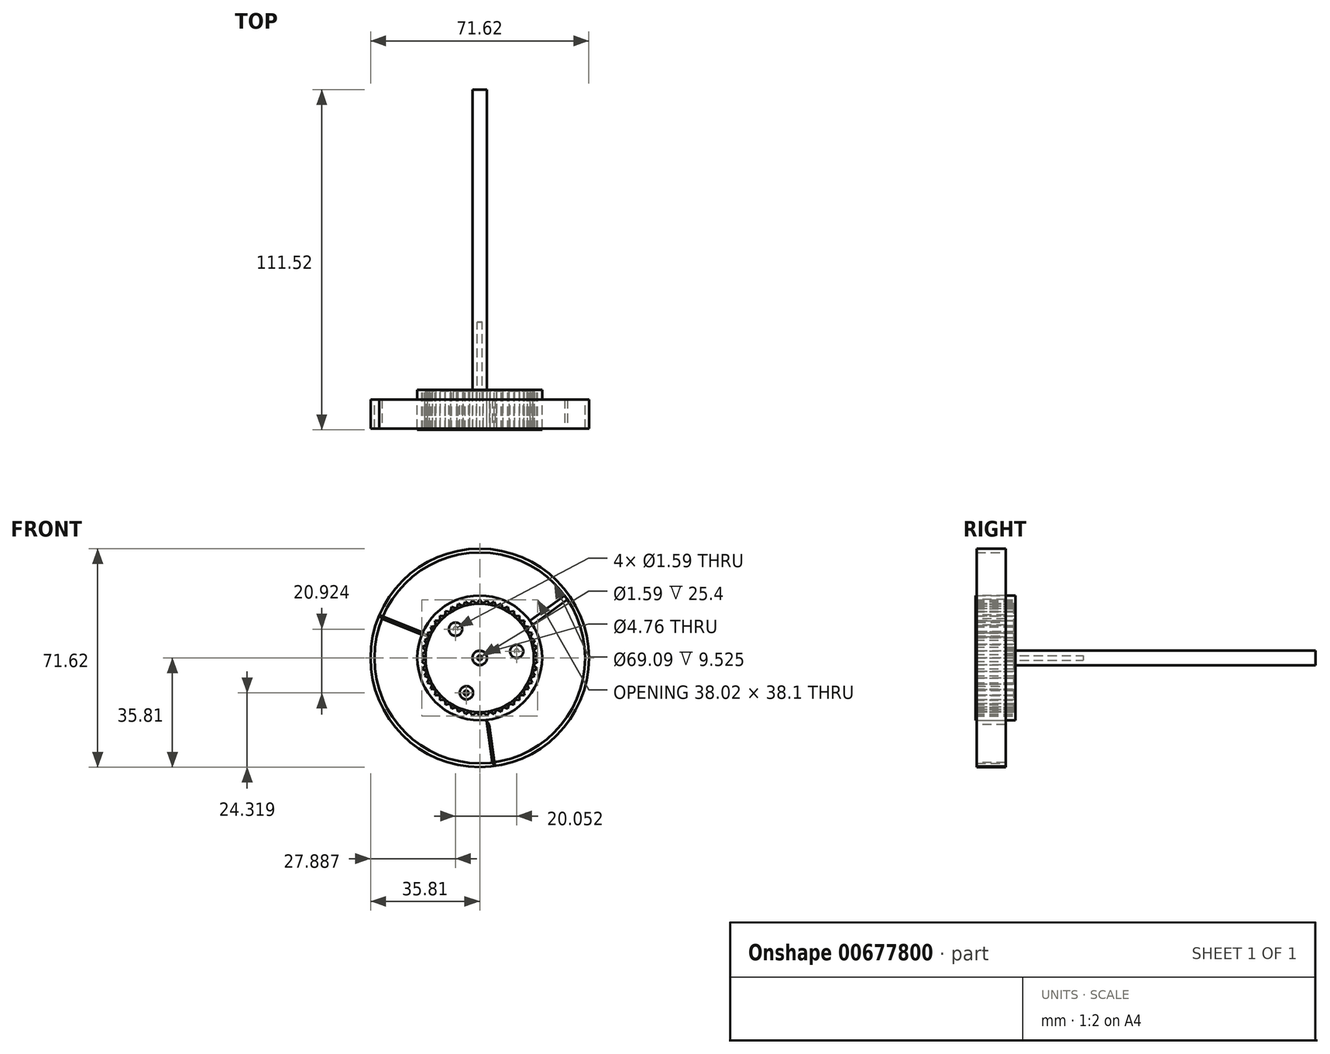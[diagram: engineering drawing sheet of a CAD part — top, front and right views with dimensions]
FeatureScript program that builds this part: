
annotation { "Feature Type Name" : "Feature", "Feature Type Description" : "" }
export const myFeature = defineFeature(function(context is Context, id is Id, definition is map)
    precondition{}
    {
        {
            var Q0;
            Q0=qCreatedBy(makeId("Front.planeOp"),FACE);
            var sketch = newSketch(context, id + "F0", { "sketchPlane" : qUnion([Q0])});
            skCircle(sketch, "E0.cCircle", {"center": v(0, 0) * mm, "radius": 19.01 * mm, "construction": true});
            skLineSegment(sketch, "E0.0", {"start": v(19.01, 1.2) * mm, "end": v(19.01, -1.2) * mm});
            skLineSegment(sketch, "E0.1", {"start": v(19.01, -1.2) * mm, "end": v(18.71, -3.57) * mm});
            skLineSegment(sketch, "E0.2", {"start": v(18.71, -3.57) * mm, "end": v(18.12, -5.89) * mm});
            skLineSegment(sketch, "E0.3", {"start": v(18.12, -5.89) * mm, "end": v(17.24, -8.11) * mm});
            skLineSegment(sketch, "E0.4", {"start": v(17.24, -8.11) * mm, "end": v(16.08, -10.2) * mm});
            skLineSegment(sketch, "E0.5", {"start": v(16.08, -10.2) * mm, "end": v(14.68, -12.14) * mm});
            skLineSegment(sketch, "E0.6", {"start": v(14.68, -12.14) * mm, "end": v(13.04, -13.89) * mm});
            skLineSegment(sketch, "E0.7", {"start": v(13.04, -13.89) * mm, "end": v(11.2, -15.41) * mm});
            skLineSegment(sketch, "E0.8", {"start": v(11.2, -15.41) * mm, "end": v(9.18, -16.7) * mm});
            skLineSegment(sketch, "E0.9", {"start": v(9.18, -16.7) * mm, "end": v(7.01, -17.71) * mm});
            skLineSegment(sketch, "E0.10", {"start": v(7.01, -17.71) * mm, "end": v(4.74, -18.45) * mm});
            skLineSegment(sketch, "E0.11", {"start": v(4.74, -18.45) * mm, "end": v(2.39, -18.9) * mm});
            skLineSegment(sketch, "E0.12", {"start": v(2.39, -18.9) * mm, "end": v(0, -19.05) * mm});
            skLineSegment(sketch, "E0.13", {"start": v(0, -19.05) * mm, "end": v(-2.39, -18.9) * mm});
            skLineSegment(sketch, "E0.14", {"start": v(-2.39, -18.9) * mm, "end": v(-4.74, -18.45) * mm});
            skLineSegment(sketch, "E0.15", {"start": v(-4.74, -18.45) * mm, "end": v(-7.01, -17.71) * mm});
            skLineSegment(sketch, "E0.16", {"start": v(-7.01, -17.71) * mm, "end": v(-9.18, -16.7) * mm});
            skLineSegment(sketch, "E0.17", {"start": v(-9.18, -16.7) * mm, "end": v(-11.2, -15.41) * mm});
            skLineSegment(sketch, "E0.18", {"start": v(-11.2, -15.41) * mm, "end": v(-13.04, -13.89) * mm});
            skLineSegment(sketch, "E0.19", {"start": v(-13.04, -13.89) * mm, "end": v(-14.68, -12.14) * mm});
            skLineSegment(sketch, "E0.20", {"start": v(-14.68, -12.14) * mm, "end": v(-16.08, -10.2) * mm});
            skLineSegment(sketch, "E0.21", {"start": v(-16.08, -10.2) * mm, "end": v(-17.24, -8.11) * mm});
            skLineSegment(sketch, "E0.22", {"start": v(-17.24, -8.11) * mm, "end": v(-18.12, -5.89) * mm});
            skLineSegment(sketch, "E0.23", {"start": v(-18.12, -5.89) * mm, "end": v(-18.71, -3.57) * mm});
            skLineSegment(sketch, "E0.24", {"start": v(-18.71, -3.57) * mm, "end": v(-19.01, -1.2) * mm});
            skLineSegment(sketch, "E0.25", {"start": v(-19.01, -1.2) * mm, "end": v(-19.01, 1.2) * mm});
            skLineSegment(sketch, "E0.26", {"start": v(-19.01, 1.2) * mm, "end": v(-18.71, 3.57) * mm});
            skLineSegment(sketch, "E0.27", {"start": v(-18.71, 3.57) * mm, "end": v(-18.12, 5.89) * mm});
            skLineSegment(sketch, "E0.28", {"start": v(-18.12, 5.89) * mm, "end": v(-17.24, 8.11) * mm});
            skLineSegment(sketch, "E0.29", {"start": v(-17.24, 8.11) * mm, "end": v(-16.08, 10.2) * mm});
            skLineSegment(sketch, "E0.30", {"start": v(-16.08, 10.2) * mm, "end": v(-14.68, 12.14) * mm});
            skLineSegment(sketch, "E0.31", {"start": v(-14.68, 12.14) * mm, "end": v(-13.04, 13.89) * mm});
            skLineSegment(sketch, "E0.32", {"start": v(-13.04, 13.89) * mm, "end": v(-11.2, 15.41) * mm});
            skLineSegment(sketch, "E0.33", {"start": v(-11.2, 15.41) * mm, "end": v(-9.18, 16.7) * mm});
            skLineSegment(sketch, "E0.34", {"start": v(-9.18, 16.7) * mm, "end": v(-7.01, 17.71) * mm});
            skLineSegment(sketch, "E0.35", {"start": v(-7.01, 17.71) * mm, "end": v(-4.74, 18.45) * mm});
            skLineSegment(sketch, "E0.36", {"start": v(-4.74, 18.45) * mm, "end": v(-2.39, 18.9) * mm});
            skLineSegment(sketch, "E0.37", {"start": v(-2.39, 18.9) * mm, "end": v(0, 19.05) * mm});
            skLineSegment(sketch, "E0.38", {"start": v(0, 19.05) * mm, "end": v(2.39, 18.9) * mm});
            skLineSegment(sketch, "E0.39", {"start": v(2.39, 18.9) * mm, "end": v(4.74, 18.45) * mm});
            skLineSegment(sketch, "E0.40", {"start": v(4.74, 18.45) * mm, "end": v(7.01, 17.71) * mm});
            skLineSegment(sketch, "E0.41", {"start": v(7.01, 17.71) * mm, "end": v(9.18, 16.7) * mm});
            skLineSegment(sketch, "E0.42", {"start": v(9.18, 16.7) * mm, "end": v(11.2, 15.41) * mm});
            skLineSegment(sketch, "E0.43", {"start": v(11.2, 15.41) * mm, "end": v(13.04, 13.89) * mm});
            skLineSegment(sketch, "E0.44", {"start": v(13.04, 13.89) * mm, "end": v(14.68, 12.14) * mm});
            skLineSegment(sketch, "E0.45", {"start": v(14.68, 12.14) * mm, "end": v(16.08, 10.2) * mm});
            skLineSegment(sketch, "E0.46", {"start": v(16.08, 10.2) * mm, "end": v(17.24, 8.11) * mm});
            skLineSegment(sketch, "E0.47", {"start": v(17.24, 8.11) * mm, "end": v(18.12, 5.89) * mm});
            skLineSegment(sketch, "E0.48", {"start": v(18.12, 5.89) * mm, "end": v(18.71, 3.57) * mm});
            skLineSegment(sketch, "E0.49", {"start": v(18.71, 3.57) * mm, "end": v(19.01, 1.2) * mm});
            skPoint(sketch, "E0.0.midPoint", {"position": v(19.01, 0) * mm});
            skCircle(sketch, "E1", {"center": v(0, 0) * mm, "radius": 20.47 * mm});
            skCircle(sketch, "E2", {"center": v(0, 0) * mm, "radius": 2.38 * mm});
            skCircle(sketch, "E3", {"center": v(0, 0) * mm, "radius": 17.76 * mm});
            skSolve(sketch);
        }
        {
            var Q0;
            Q0=makeQuery(id+"F0.imprint","IMPRINT",FACE,{"disambiguationData":[TD([[makeQuery(id+"F0.imprint","IMPRINT",EDGE,{"derivedFrom":sQuery(id+"F0.wireOp",EDGE,"E0.0")}),1.0]])]});
            extrude(context, id + "F1", {"entities" : qUnion([Q0]), "depth" : 9.92 * mm, "offsetDistance" : 25.4 * mm});
        }
        {
            var Q0;
            Q0=makeQuery(id+"F0.imprint","IMPRINT",FACE,{"disambiguationData":[TD([[makeQuery(id+"F0.imprint","IMPRINT",EDGE,{"derivedFrom":sQuery(id+"F0.wireOp",EDGE,"E0.0")}),1.0]])]});
            extrude(context, id + "F2", {"entities" : qUnion([Q0]), "operationType" : NewBodyOperationType.ADD, "oppositeDirection" : true, "depth" : 3.17 * mm, "offsetDistance" : 25.4 * mm});
        }
        {
            var Q0;
            Q0=makeQuery(id+"F0.imprint","IMPRINT",FACE,{"disambiguationData":[TD([[makeQuery(id+"F0.imprint","IMPRINT",EDGE,{"derivedFrom":sQuery(id+"F0.wireOp",EDGE,"E2")}),1.0]])]});
            extrude(context, id + "F3", {"entities" : qUnion([Q0]), "oppositeDirection" : true, "depth" : 101.6 * mm, "offsetDistance" : 25.4 * mm});
        }
        {
            var Q0;
            {var subQ0=sQuery(id+"F0.wireOp",EDGE,"E0.9");Q0=makeQuery(id+"F2.boolean.opBoolean","MERGE",FACE,{"derivedFrom":[makeQuery(id+"F1.opExtrude","SWEPT_FACE",FACE,{"disambiguationData":[OSD([subQ0])]}),makeQuery(id+"F2.opExtrude","SWEPT_FACE",FACE,{"disambiguationData":[OSD([subQ0])]})]});}
            extrude(context, id + "F4", {"entities" : qUnion([Q0]), "operationType" : NewBodyOperationType.ADD, "depth" : 1.2 * mm, "offsetDistance" : 25.4 * mm});
        }
        {
            var Q0;
            {var subQ0=sQuery(id+"F0.wireOp",EDGE,"E0.11");Q0=makeQuery(id+"F2.boolean.opBoolean","MERGE",FACE,{"derivedFrom":[makeQuery(id+"F1.opExtrude","SWEPT_FACE",FACE,{"disambiguationData":[OSD([subQ0])]}),makeQuery(id+"F2.opExtrude","SWEPT_FACE",FACE,{"disambiguationData":[OSD([subQ0])]})]});}
            extrude(context, id + "F5", {"entities" : qUnion([Q0]), "operationType" : NewBodyOperationType.ADD, "depth" : 1.2 * mm, "offsetDistance" : 25.4 * mm});
        }
        {
            var Q0;
            {var subQ0=sQuery(id+"F0.wireOp",EDGE,"E0.13");Q0=makeQuery(id+"F2.boolean.opBoolean","MERGE",FACE,{"derivedFrom":[makeQuery(id+"F1.opExtrude","SWEPT_FACE",FACE,{"disambiguationData":[OSD([subQ0])]}),makeQuery(id+"F2.opExtrude","SWEPT_FACE",FACE,{"disambiguationData":[OSD([subQ0])]})]});}
            extrude(context, id + "F6", {"entities" : qUnion([Q0]), "operationType" : NewBodyOperationType.ADD, "depth" : 1.2 * mm, "offsetDistance" : 25.4 * mm});
        }
        {
            var Q0;
            {var subQ0=sQuery(id+"F0.wireOp",EDGE,"E0.7");Q0=makeQuery(id+"F2.boolean.opBoolean","MERGE",FACE,{"derivedFrom":[makeQuery(id+"F1.opExtrude","SWEPT_FACE",FACE,{"disambiguationData":[OSD([subQ0])]}),makeQuery(id+"F2.opExtrude","SWEPT_FACE",FACE,{"disambiguationData":[OSD([subQ0])]})]});}
            extrude(context, id + "F7", {"entities" : qUnion([Q0]), "operationType" : NewBodyOperationType.ADD, "depth" : 1.2 * mm, "offsetDistance" : 25.4 * mm});
        }
        {
            var Q0;
            {var subQ0=sQuery(id+"F0.wireOp",EDGE,"E0.5");Q0=makeQuery(id+"F2.boolean.opBoolean","MERGE",FACE,{"derivedFrom":[makeQuery(id+"F1.opExtrude","SWEPT_FACE",FACE,{"disambiguationData":[OSD([subQ0])]}),makeQuery(id+"F2.opExtrude","SWEPT_FACE",FACE,{"disambiguationData":[OSD([subQ0])]})]});}
            extrude(context, id + "F8", {"entities" : qUnion([Q0]), "operationType" : NewBodyOperationType.ADD, "depth" : 1.2 * mm, "offsetDistance" : 25.4 * mm});
        }
        {
            var Q0;
            {var subQ0=sQuery(id+"F0.wireOp",EDGE,"E0.3");Q0=makeQuery(id+"F2.boolean.opBoolean","MERGE",FACE,{"derivedFrom":[makeQuery(id+"F1.opExtrude","SWEPT_FACE",FACE,{"disambiguationData":[OSD([subQ0])]}),makeQuery(id+"F2.opExtrude","SWEPT_FACE",FACE,{"disambiguationData":[OSD([subQ0])]})]});}
            extrude(context, id + "F9", {"entities" : qUnion([Q0]), "operationType" : NewBodyOperationType.ADD, "depth" : 1.2 * mm, "offsetDistance" : 25.4 * mm});
        }
        {
            var Q0;
            {var subQ0=sQuery(id+"F0.wireOp",EDGE,"E0.1");Q0=makeQuery(id+"F2.boolean.opBoolean","MERGE",FACE,{"derivedFrom":[makeQuery(id+"F1.opExtrude","SWEPT_FACE",FACE,{"disambiguationData":[OSD([subQ0])]}),makeQuery(id+"F2.opExtrude","SWEPT_FACE",FACE,{"disambiguationData":[OSD([subQ0])]})]});}
            extrude(context, id + "F10", {"entities" : qUnion([Q0]), "operationType" : NewBodyOperationType.ADD, "depth" : 1.2 * mm, "offsetDistance" : 25.4 * mm});
        }
        {
            var Q0;
            {var subQ0=sQuery(id+"F0.wireOp",EDGE,"E0.49");Q0=makeQuery(id+"F2.boolean.opBoolean","MERGE",FACE,{"derivedFrom":[makeQuery(id+"F1.opExtrude","SWEPT_FACE",FACE,{"disambiguationData":[OSD([subQ0])]}),makeQuery(id+"F2.opExtrude","SWEPT_FACE",FACE,{"disambiguationData":[OSD([subQ0])]})]});}
            extrude(context, id + "F11", {"entities" : qUnion([Q0]), "operationType" : NewBodyOperationType.ADD, "depth" : 1.2 * mm, "offsetDistance" : 25.4 * mm});
        }
        {
            var Q0;
            {var subQ0=sQuery(id+"F0.wireOp",EDGE,"E0.47");Q0=makeQuery(id+"F2.boolean.opBoolean","MERGE",FACE,{"derivedFrom":[makeQuery(id+"F1.opExtrude","SWEPT_FACE",FACE,{"disambiguationData":[OSD([subQ0])]}),makeQuery(id+"F2.opExtrude","SWEPT_FACE",FACE,{"disambiguationData":[OSD([subQ0])]})]});}
            extrude(context, id + "F12", {"entities" : qUnion([Q0]), "operationType" : NewBodyOperationType.ADD, "depth" : 1.2 * mm, "offsetDistance" : 25.4 * mm});
        }
        {
            var Q0;
            {var subQ0=sQuery(id+"F0.wireOp",EDGE,"E0.45");Q0=makeQuery(id+"F2.boolean.opBoolean","MERGE",FACE,{"derivedFrom":[makeQuery(id+"F1.opExtrude","SWEPT_FACE",FACE,{"disambiguationData":[OSD([subQ0])]}),makeQuery(id+"F2.opExtrude","SWEPT_FACE",FACE,{"disambiguationData":[OSD([subQ0])]})]});}
            extrude(context, id + "F13", {"entities" : qUnion([Q0]), "operationType" : NewBodyOperationType.ADD, "depth" : 1.2 * mm, "offsetDistance" : 25.4 * mm});
        }
        {
            var Q0;
            {var subQ0=sQuery(id+"F0.wireOp",EDGE,"E0.43");Q0=makeQuery(id+"F2.boolean.opBoolean","MERGE",FACE,{"derivedFrom":[makeQuery(id+"F1.opExtrude","SWEPT_FACE",FACE,{"disambiguationData":[OSD([subQ0])]}),makeQuery(id+"F2.opExtrude","SWEPT_FACE",FACE,{"disambiguationData":[OSD([subQ0])]})]});}
            extrude(context, id + "F14", {"entities" : qUnion([Q0]), "operationType" : NewBodyOperationType.ADD, "depth" : 1.2 * mm, "offsetDistance" : 25.4 * mm});
        }
        {
            var Q0;
            {var subQ0=sQuery(id+"F0.wireOp",EDGE,"E0.41");Q0=makeQuery(id+"F2.boolean.opBoolean","MERGE",FACE,{"derivedFrom":[makeQuery(id+"F1.opExtrude","SWEPT_FACE",FACE,{"disambiguationData":[OSD([subQ0])]}),makeQuery(id+"F2.opExtrude","SWEPT_FACE",FACE,{"disambiguationData":[OSD([subQ0])]})]});}
            extrude(context, id + "F15", {"entities" : qUnion([Q0]), "operationType" : NewBodyOperationType.ADD, "depth" : 1.2 * mm, "offsetDistance" : 25.4 * mm});
        }
        {
            var Q0;
            {var subQ0=sQuery(id+"F0.wireOp",EDGE,"E0.39");Q0=makeQuery(id+"F2.boolean.opBoolean","MERGE",FACE,{"derivedFrom":[makeQuery(id+"F1.opExtrude","SWEPT_FACE",FACE,{"disambiguationData":[OSD([subQ0])]}),makeQuery(id+"F2.opExtrude","SWEPT_FACE",FACE,{"disambiguationData":[OSD([subQ0])]})]});}
            extrude(context, id + "F16", {"entities" : qUnion([Q0]), "operationType" : NewBodyOperationType.ADD, "depth" : 1.2 * mm, "offsetDistance" : 25.4 * mm});
        }
        {
            var Q0;
            {var subQ0=sQuery(id+"F0.wireOp",EDGE,"E0.37");Q0=makeQuery(id+"F2.boolean.opBoolean","MERGE",FACE,{"derivedFrom":[makeQuery(id+"F1.opExtrude","SWEPT_FACE",FACE,{"disambiguationData":[OSD([subQ0])]}),makeQuery(id+"F2.opExtrude","SWEPT_FACE",FACE,{"disambiguationData":[OSD([subQ0])]})]});}
            extrude(context, id + "F17", {"entities" : qUnion([Q0]), "operationType" : NewBodyOperationType.ADD, "depth" : 1.2 * mm, "offsetDistance" : 25.4 * mm});
        }
        {
            var Q0;
            {var subQ0=sQuery(id+"F0.wireOp",EDGE,"E0.35");Q0=makeQuery(id+"F2.boolean.opBoolean","MERGE",FACE,{"derivedFrom":[makeQuery(id+"F1.opExtrude","SWEPT_FACE",FACE,{"disambiguationData":[OSD([subQ0])]}),makeQuery(id+"F2.opExtrude","SWEPT_FACE",FACE,{"disambiguationData":[OSD([subQ0])]})]});}
            extrude(context, id + "F18", {"entities" : qUnion([Q0]), "operationType" : NewBodyOperationType.ADD, "depth" : 1.2 * mm, "offsetDistance" : 25.4 * mm});
        }
        {
            var Q0;
            {var subQ0=sQuery(id+"F0.wireOp",EDGE,"E0.33");Q0=makeQuery(id+"F2.boolean.opBoolean","MERGE",FACE,{"derivedFrom":[makeQuery(id+"F1.opExtrude","SWEPT_FACE",FACE,{"disambiguationData":[OSD([subQ0])]}),makeQuery(id+"F2.opExtrude","SWEPT_FACE",FACE,{"disambiguationData":[OSD([subQ0])]})]});}
            extrude(context, id + "F19", {"entities" : qUnion([Q0]), "operationType" : NewBodyOperationType.ADD, "depth" : 1.2 * mm, "offsetDistance" : 25.4 * mm});
        }
        {
            var Q0;
            {var subQ0=sQuery(id+"F0.wireOp",EDGE,"E0.31");Q0=makeQuery(id+"F2.boolean.opBoolean","MERGE",FACE,{"derivedFrom":[makeQuery(id+"F1.opExtrude","SWEPT_FACE",FACE,{"disambiguationData":[OSD([subQ0])]}),makeQuery(id+"F2.opExtrude","SWEPT_FACE",FACE,{"disambiguationData":[OSD([subQ0])]})]});}
            extrude(context, id + "F20", {"entities" : qUnion([Q0]), "operationType" : NewBodyOperationType.ADD, "depth" : 1.2 * mm, "offsetDistance" : 25.4 * mm});
        }
        {
            var Q0;
            {var subQ0=sQuery(id+"F0.wireOp",EDGE,"E0.29");Q0=makeQuery(id+"F2.boolean.opBoolean","MERGE",FACE,{"derivedFrom":[makeQuery(id+"F1.opExtrude","SWEPT_FACE",FACE,{"disambiguationData":[OSD([subQ0])]}),makeQuery(id+"F2.opExtrude","SWEPT_FACE",FACE,{"disambiguationData":[OSD([subQ0])]})]});}
            extrude(context, id + "F21", {"entities" : qUnion([Q0]), "operationType" : NewBodyOperationType.ADD, "depth" : 1.2 * mm, "offsetDistance" : 25.4 * mm});
        }
        {
            var Q0;
            {var subQ0=sQuery(id+"F0.wireOp",EDGE,"E0.27");Q0=makeQuery(id+"F2.boolean.opBoolean","MERGE",FACE,{"derivedFrom":[makeQuery(id+"F1.opExtrude","SWEPT_FACE",FACE,{"disambiguationData":[OSD([subQ0])]}),makeQuery(id+"F2.opExtrude","SWEPT_FACE",FACE,{"disambiguationData":[OSD([subQ0])]})]});}
            extrude(context, id + "F22", {"entities" : qUnion([Q0]), "operationType" : NewBodyOperationType.ADD, "depth" : 1.2 * mm, "offsetDistance" : 25.4 * mm});
        }
        {
            var Q0;
            {var subQ0=sQuery(id+"F0.wireOp",EDGE,"E0.25");Q0=makeQuery(id+"F2.boolean.opBoolean","MERGE",FACE,{"derivedFrom":[makeQuery(id+"F1.opExtrude","SWEPT_FACE",FACE,{"disambiguationData":[OSD([subQ0])]}),makeQuery(id+"F2.opExtrude","SWEPT_FACE",FACE,{"disambiguationData":[OSD([subQ0])]})]});}
            extrude(context, id + "F23", {"entities" : qUnion([Q0]), "operationType" : NewBodyOperationType.ADD, "depth" : 1.2 * mm, "offsetDistance" : 25.4 * mm});
        }
        {
            var Q0;
            {var subQ0=sQuery(id+"F0.wireOp",EDGE,"E0.23");Q0=makeQuery(id+"F2.boolean.opBoolean","MERGE",FACE,{"derivedFrom":[makeQuery(id+"F1.opExtrude","SWEPT_FACE",FACE,{"disambiguationData":[OSD([subQ0])]}),makeQuery(id+"F2.opExtrude","SWEPT_FACE",FACE,{"disambiguationData":[OSD([subQ0])]})]});}
            extrude(context, id + "F24", {"entities" : qUnion([Q0]), "operationType" : NewBodyOperationType.ADD, "depth" : 1.2 * mm, "offsetDistance" : 25.4 * mm});
        }
        {
            var Q0;
            {var subQ0=sQuery(id+"F0.wireOp",EDGE,"E0.21");Q0=makeQuery(id+"F2.boolean.opBoolean","MERGE",FACE,{"derivedFrom":[makeQuery(id+"F1.opExtrude","SWEPT_FACE",FACE,{"disambiguationData":[OSD([subQ0])]}),makeQuery(id+"F2.opExtrude","SWEPT_FACE",FACE,{"disambiguationData":[OSD([subQ0])]})]});}
            extrude(context, id + "F25", {"entities" : qUnion([Q0]), "operationType" : NewBodyOperationType.ADD, "depth" : 1.2 * mm, "offsetDistance" : 25.4 * mm});
        }
        {
            var Q0;
            {var subQ0=sQuery(id+"F0.wireOp",EDGE,"E0.19");Q0=makeQuery(id+"F2.boolean.opBoolean","MERGE",FACE,{"derivedFrom":[makeQuery(id+"F1.opExtrude","SWEPT_FACE",FACE,{"disambiguationData":[OSD([subQ0])]}),makeQuery(id+"F2.opExtrude","SWEPT_FACE",FACE,{"disambiguationData":[OSD([subQ0])]})]});}
            extrude(context, id + "F26", {"entities" : qUnion([Q0]), "operationType" : NewBodyOperationType.ADD, "depth" : 1.2 * mm, "offsetDistance" : 25.4 * mm});
        }
        {
            var Q0;
            {var subQ0=sQuery(id+"F0.wireOp",EDGE,"E0.17");Q0=makeQuery(id+"F2.boolean.opBoolean","MERGE",FACE,{"derivedFrom":[makeQuery(id+"F1.opExtrude","SWEPT_FACE",FACE,{"disambiguationData":[OSD([subQ0])]}),makeQuery(id+"F2.opExtrude","SWEPT_FACE",FACE,{"disambiguationData":[OSD([subQ0])]})]});}
            extrude(context, id + "F27", {"entities" : qUnion([Q0]), "operationType" : NewBodyOperationType.ADD, "depth" : 1.2 * mm, "offsetDistance" : 25.4 * mm});
        }
        {
            var Q0;
            {var subQ0=sQuery(id+"F0.wireOp",EDGE,"E0.15");Q0=makeQuery(id+"F2.boolean.opBoolean","MERGE",FACE,{"derivedFrom":[makeQuery(id+"F1.opExtrude","SWEPT_FACE",FACE,{"disambiguationData":[OSD([subQ0])]}),makeQuery(id+"F2.opExtrude","SWEPT_FACE",FACE,{"disambiguationData":[OSD([subQ0])]})]});}
            extrude(context, id + "F28", {"entities" : qUnion([Q0]), "operationType" : NewBodyOperationType.ADD, "depth" : 1.2 * mm, "offsetDistance" : 25.4 * mm});
        }
        {
            var Q0;
            Q0=makeQuery(id+"F6.opExtrude","CAP_EDGE",EDGE,{"disambiguationData":[OSD([sQuery(id+"F0.wireOp",EDGE,"E0.12"),sQuery(id+"F0.wireOp",EDGE,"E0.13")])],"isStart":false});
            var Q1;
            Q1=makeQuery(id+"F6.opExtrude","CAP_EDGE",EDGE,{"disambiguationData":[OSD([sQuery(id+"F0.wireOp",EDGE,"E0.13"),sQuery(id+"F0.wireOp",EDGE,"E0.14")])],"isStart":false});
            var Q2;
            Q2=makeQuery(id+"F5.opExtrude","CAP_EDGE",EDGE,{"disambiguationData":[OSD([sQuery(id+"F0.wireOp",EDGE,"E0.11"),sQuery(id+"F0.wireOp",EDGE,"E0.12")])],"isStart":false});
            var Q3;
            Q3=makeQuery(id+"F5.opExtrude","CAP_EDGE",EDGE,{"disambiguationData":[OSD([sQuery(id+"F0.wireOp",EDGE,"E0.10"),sQuery(id+"F0.wireOp",EDGE,"E0.11")])],"isStart":false});
            var Q4;
            Q4=makeQuery(id+"F4.opExtrude","CAP_EDGE",EDGE,{"disambiguationData":[OSD([sQuery(id+"F0.wireOp",EDGE,"E0.9"),sQuery(id+"F0.wireOp",EDGE,"E0.10")])],"isStart":false});
            var Q5;
            Q5=makeQuery(id+"F4.opExtrude","CAP_EDGE",EDGE,{"disambiguationData":[OSD([sQuery(id+"F0.wireOp",EDGE,"E0.8"),sQuery(id+"F0.wireOp",EDGE,"E0.9")])],"isStart":false});
            var Q6;
            Q6=makeQuery(id+"F7.opExtrude","CAP_EDGE",EDGE,{"disambiguationData":[OSD([sQuery(id+"F0.wireOp",EDGE,"E0.6"),sQuery(id+"F0.wireOp",EDGE,"E0.7")])],"isStart":false});
            var Q7;
            Q7=makeQuery(id+"F7.opExtrude","CAP_EDGE",EDGE,{"disambiguationData":[OSD([sQuery(id+"F0.wireOp",EDGE,"E0.7"),sQuery(id+"F0.wireOp",EDGE,"E0.8")])],"isStart":false});
            var Q8;
            Q8=makeQuery(id+"F8.opExtrude","CAP_EDGE",EDGE,{"disambiguationData":[OSD([sQuery(id+"F0.wireOp",EDGE,"E0.5"),sQuery(id+"F0.wireOp",EDGE,"E0.6")])],"isStart":false});
            var Q9;
            Q9=makeQuery(id+"F8.opExtrude","CAP_EDGE",EDGE,{"disambiguationData":[OSD([sQuery(id+"F0.wireOp",EDGE,"E0.4"),sQuery(id+"F0.wireOp",EDGE,"E0.5")])],"isStart":false});
            var Q10;
            Q10=makeQuery(id+"F9.opExtrude","CAP_EDGE",EDGE,{"disambiguationData":[OSD([sQuery(id+"F0.wireOp",EDGE,"E0.2"),sQuery(id+"F0.wireOp",EDGE,"E0.3")])],"isStart":false});
            var Q11;
            Q11=makeQuery(id+"F9.opExtrude","CAP_EDGE",EDGE,{"disambiguationData":[OSD([sQuery(id+"F0.wireOp",EDGE,"E0.3"),sQuery(id+"F0.wireOp",EDGE,"E0.4")])],"isStart":false});
            var Q12;
            Q12=makeQuery(id+"F10.opExtrude","CAP_EDGE",EDGE,{"disambiguationData":[OSD([sQuery(id+"F0.wireOp",EDGE,"E0.1"),sQuery(id+"F0.wireOp",EDGE,"E0.2")])],"isStart":false});
            var Q13;
            Q13=makeQuery(id+"F10.opExtrude","CAP_EDGE",EDGE,{"disambiguationData":[OSD([sQuery(id+"F0.wireOp",EDGE,"E0.0"),sQuery(id+"F0.wireOp",EDGE,"E0.1")])],"isStart":false});
            var Q14;
            Q14=makeQuery(id+"F11.opExtrude","CAP_EDGE",EDGE,{"disambiguationData":[OSD([sQuery(id+"F0.wireOp",EDGE,"E0.48"),sQuery(id+"F0.wireOp",EDGE,"E0.49")])],"isStart":false});
            var Q15;
            Q15=makeQuery(id+"F11.opExtrude","CAP_EDGE",EDGE,{"disambiguationData":[OSD([sQuery(id+"F0.wireOp",EDGE,"E0.0"),sQuery(id+"F0.wireOp",EDGE,"E0.49")])],"isStart":false});
            var Q16;
            Q16=makeQuery(id+"F12.opExtrude","CAP_EDGE",EDGE,{"disambiguationData":[OSD([sQuery(id+"F0.wireOp",EDGE,"E0.47"),sQuery(id+"F0.wireOp",EDGE,"E0.48")])],"isStart":false});
            var Q17;
            Q17=makeQuery(id+"F12.opExtrude","CAP_EDGE",EDGE,{"disambiguationData":[OSD([sQuery(id+"F0.wireOp",EDGE,"E0.46"),sQuery(id+"F0.wireOp",EDGE,"E0.47")])],"isStart":false});
            var Q18;
            Q18=makeQuery(id+"F13.opExtrude","CAP_EDGE",EDGE,{"disambiguationData":[OSD([sQuery(id+"F0.wireOp",EDGE,"E0.45"),sQuery(id+"F0.wireOp",EDGE,"E0.46")])],"isStart":false});
            var Q19;
            Q19=makeQuery(id+"F13.opExtrude","CAP_EDGE",EDGE,{"disambiguationData":[OSD([sQuery(id+"F0.wireOp",EDGE,"E0.44"),sQuery(id+"F0.wireOp",EDGE,"E0.45")])],"isStart":false});
            var Q20;
            Q20=makeQuery(id+"F14.opExtrude","CAP_EDGE",EDGE,{"disambiguationData":[OSD([sQuery(id+"F0.wireOp",EDGE,"E0.43"),sQuery(id+"F0.wireOp",EDGE,"E0.44")])],"isStart":false});
            var Q21;
            Q21=makeQuery(id+"F14.opExtrude","CAP_EDGE",EDGE,{"disambiguationData":[OSD([sQuery(id+"F0.wireOp",EDGE,"E0.42"),sQuery(id+"F0.wireOp",EDGE,"E0.43")])],"isStart":false});
            var Q22;
            Q22=makeQuery(id+"F15.opExtrude","CAP_EDGE",EDGE,{"disambiguationData":[OSD([sQuery(id+"F0.wireOp",EDGE,"E0.41"),sQuery(id+"F0.wireOp",EDGE,"E0.42")])],"isStart":false});
            var Q23;
            Q23=makeQuery(id+"F15.opExtrude","CAP_EDGE",EDGE,{"disambiguationData":[OSD([sQuery(id+"F0.wireOp",EDGE,"E0.40"),sQuery(id+"F0.wireOp",EDGE,"E0.41")])],"isStart":false});
            var Q24;
            Q24=makeQuery(id+"F16.opExtrude","CAP_EDGE",EDGE,{"disambiguationData":[OSD([sQuery(id+"F0.wireOp",EDGE,"E0.39"),sQuery(id+"F0.wireOp",EDGE,"E0.40")])],"isStart":false});
            var Q25;
            Q25=makeQuery(id+"F16.opExtrude","CAP_EDGE",EDGE,{"disambiguationData":[OSD([sQuery(id+"F0.wireOp",EDGE,"E0.38"),sQuery(id+"F0.wireOp",EDGE,"E0.39")])],"isStart":false});
            var Q26;
            Q26=makeQuery(id+"F17.opExtrude","CAP_EDGE",EDGE,{"disambiguationData":[OSD([sQuery(id+"F0.wireOp",EDGE,"E0.37"),sQuery(id+"F0.wireOp",EDGE,"E0.38")])],"isStart":false});
            var Q27;
            Q27=makeQuery(id+"F17.opExtrude","CAP_EDGE",EDGE,{"disambiguationData":[OSD([sQuery(id+"F0.wireOp",EDGE,"E0.36"),sQuery(id+"F0.wireOp",EDGE,"E0.37")])],"isStart":false});
            var Q28;
            Q28=makeQuery(id+"F18.opExtrude","CAP_EDGE",EDGE,{"disambiguationData":[OSD([sQuery(id+"F0.wireOp",EDGE,"E0.35"),sQuery(id+"F0.wireOp",EDGE,"E0.36")])],"isStart":false});
            var Q29;
            Q29=makeQuery(id+"F18.opExtrude","CAP_EDGE",EDGE,{"disambiguationData":[OSD([sQuery(id+"F0.wireOp",EDGE,"E0.34"),sQuery(id+"F0.wireOp",EDGE,"E0.35")])],"isStart":false});
            var Q30;
            Q30=makeQuery(id+"F19.opExtrude","CAP_EDGE",EDGE,{"disambiguationData":[OSD([sQuery(id+"F0.wireOp",EDGE,"E0.32"),sQuery(id+"F0.wireOp",EDGE,"E0.33")])],"isStart":false});
            var Q31;
            Q31=makeQuery(id+"F19.opExtrude","CAP_EDGE",EDGE,{"disambiguationData":[OSD([sQuery(id+"F0.wireOp",EDGE,"E0.33"),sQuery(id+"F0.wireOp",EDGE,"E0.34")])],"isStart":false});
            var Q32;
            Q32=makeQuery(id+"F20.opExtrude","CAP_EDGE",EDGE,{"disambiguationData":[OSD([sQuery(id+"F0.wireOp",EDGE,"E0.30"),sQuery(id+"F0.wireOp",EDGE,"E0.31")])],"isStart":false});
            var Q33;
            Q33=makeQuery(id+"F20.opExtrude","CAP_EDGE",EDGE,{"disambiguationData":[OSD([sQuery(id+"F0.wireOp",EDGE,"E0.31"),sQuery(id+"F0.wireOp",EDGE,"E0.32")])],"isStart":false});
            var Q34;
            Q34=makeQuery(id+"F21.opExtrude","CAP_EDGE",EDGE,{"disambiguationData":[OSD([sQuery(id+"F0.wireOp",EDGE,"E0.29"),sQuery(id+"F0.wireOp",EDGE,"E0.30")])],"isStart":false});
            var Q35;
            Q35=makeQuery(id+"F21.opExtrude","CAP_EDGE",EDGE,{"disambiguationData":[OSD([sQuery(id+"F0.wireOp",EDGE,"E0.28"),sQuery(id+"F0.wireOp",EDGE,"E0.29")])],"isStart":false});
            var Q36;
            Q36=makeQuery(id+"F22.opExtrude","CAP_EDGE",EDGE,{"disambiguationData":[OSD([sQuery(id+"F0.wireOp",EDGE,"E0.27"),sQuery(id+"F0.wireOp",EDGE,"E0.28")])],"isStart":false});
            var Q37;
            Q37=makeQuery(id+"F22.opExtrude","CAP_EDGE",EDGE,{"disambiguationData":[OSD([sQuery(id+"F0.wireOp",EDGE,"E0.26"),sQuery(id+"F0.wireOp",EDGE,"E0.27")])],"isStart":false});
            var Q38;
            Q38=makeQuery(id+"F23.opExtrude","CAP_EDGE",EDGE,{"disambiguationData":[OSD([sQuery(id+"F0.wireOp",EDGE,"E0.25"),sQuery(id+"F0.wireOp",EDGE,"E0.26")])],"isStart":false});
            var Q39;
            Q39=makeQuery(id+"F23.opExtrude","CAP_EDGE",EDGE,{"disambiguationData":[OSD([sQuery(id+"F0.wireOp",EDGE,"E0.24"),sQuery(id+"F0.wireOp",EDGE,"E0.25")])],"isStart":false});
            var Q40;
            Q40=makeQuery(id+"F24.opExtrude","CAP_EDGE",EDGE,{"disambiguationData":[OSD([sQuery(id+"F0.wireOp",EDGE,"E0.23"),sQuery(id+"F0.wireOp",EDGE,"E0.24")])],"isStart":false});
            var Q41;
            Q41=makeQuery(id+"F24.opExtrude","CAP_EDGE",EDGE,{"disambiguationData":[OSD([sQuery(id+"F0.wireOp",EDGE,"E0.22"),sQuery(id+"F0.wireOp",EDGE,"E0.23")])],"isStart":false});
            var Q42;
            Q42=makeQuery(id+"F25.opExtrude","CAP_EDGE",EDGE,{"disambiguationData":[OSD([sQuery(id+"F0.wireOp",EDGE,"E0.21"),sQuery(id+"F0.wireOp",EDGE,"E0.22")])],"isStart":false});
            var Q43;
            Q43=makeQuery(id+"F25.opExtrude","CAP_EDGE",EDGE,{"disambiguationData":[OSD([sQuery(id+"F0.wireOp",EDGE,"E0.20"),sQuery(id+"F0.wireOp",EDGE,"E0.21")])],"isStart":false});
            var Q44;
            Q44=makeQuery(id+"F26.opExtrude","CAP_EDGE",EDGE,{"disambiguationData":[OSD([sQuery(id+"F0.wireOp",EDGE,"E0.19"),sQuery(id+"F0.wireOp",EDGE,"E0.20")])],"isStart":false});
            var Q45;
            Q45=makeQuery(id+"F26.opExtrude","CAP_EDGE",EDGE,{"disambiguationData":[OSD([sQuery(id+"F0.wireOp",EDGE,"E0.18"),sQuery(id+"F0.wireOp",EDGE,"E0.19")])],"isStart":false});
            var Q46;
            Q46=makeQuery(id+"F27.opExtrude","CAP_EDGE",EDGE,{"disambiguationData":[OSD([sQuery(id+"F0.wireOp",EDGE,"E0.16"),sQuery(id+"F0.wireOp",EDGE,"E0.17")])],"isStart":false});
            var Q47;
            Q47=makeQuery(id+"F27.opExtrude","CAP_EDGE",EDGE,{"disambiguationData":[OSD([sQuery(id+"F0.wireOp",EDGE,"E0.17"),sQuery(id+"F0.wireOp",EDGE,"E0.18")])],"isStart":false});
            chamfer(context, id + "F29", {"entities" : qUnion([Q0, Q1, Q2, Q3, Q4, Q5, Q6, Q7, Q8, Q9, Q10, Q11, Q12, Q13, Q14, Q15, Q16, Q17, Q18, Q19, Q20, Q21, Q22, Q23, Q24, Q25, Q26, Q27, Q28, Q29, Q30, Q31, Q32, Q33, Q34, Q35, Q36, Q37, Q38, Q39, Q40, Q41, Q42, Q43, Q44, Q45, Q46, Q47]), "width" : 1.2 * mm, "tangentPropagation" : true});
        }
        {
            var Q0;
            Q0=makeQuery(id+"F28.opExtrude","CAP_EDGE",EDGE,{"disambiguationData":[OSD([sQuery(id+"F0.wireOp",EDGE,"E0.14"),sQuery(id+"F0.wireOp",EDGE,"E0.15")])],"isStart":false});
            var Q1;
            Q1=makeQuery(id+"F28.opExtrude","CAP_EDGE",EDGE,{"disambiguationData":[OSD([sQuery(id+"F0.wireOp",EDGE,"E0.15"),sQuery(id+"F0.wireOp",EDGE,"E0.16")])],"isStart":false});
            chamfer(context, id + "F30", {"entities" : qUnion([Q0, Q1]), "width" : 1.2 * mm, "tangentPropagation" : true});
        }
        {
            var Q0;
            {var subQ0=sQuery(id+"F0.wireOp",EDGE,"E0.16");Q0=makeQuery(id+"F2.boolean.opBoolean","MERGE",FACE,{"derivedFrom":[makeQuery(id+"F1.opExtrude","SWEPT_FACE",FACE,{"disambiguationData":[OSD([subQ0])]}),makeQuery(id+"F2.opExtrude","SWEPT_FACE",FACE,{"disambiguationData":[OSD([subQ0])]})]});}
            extrude(context, id + "F31", {"entities" : qUnion([Q0]), "operationType" : NewBodyOperationType.ADD, "depth" : 1.2 * mm, "offsetDistance" : 25.4 * mm});
        }
        {
            var Q0;
            {var subQ0=sQuery(id+"F0.wireOp",EDGE,"E0.14");Q0=makeQuery(id+"F2.boolean.opBoolean","MERGE",FACE,{"derivedFrom":[makeQuery(id+"F1.opExtrude","SWEPT_FACE",FACE,{"disambiguationData":[OSD([subQ0])]}),makeQuery(id+"F2.opExtrude","SWEPT_FACE",FACE,{"disambiguationData":[OSD([subQ0])]})]});}
            extrude(context, id + "F32", {"entities" : qUnion([Q0]), "operationType" : NewBodyOperationType.ADD, "depth" : 1.2 * mm, "offsetDistance" : 25.4 * mm});
        }
        {
            var Q0;
            {var subQ0=sQuery(id+"F0.wireOp",EDGE,"E0.18");Q0=makeQuery(id+"F2.boolean.opBoolean","MERGE",FACE,{"derivedFrom":[makeQuery(id+"F1.opExtrude","SWEPT_FACE",FACE,{"disambiguationData":[OSD([subQ0])]}),makeQuery(id+"F2.opExtrude","SWEPT_FACE",FACE,{"disambiguationData":[OSD([subQ0])]})]});}
            extrude(context, id + "F33", {"entities" : qUnion([Q0]), "operationType" : NewBodyOperationType.ADD, "depth" : 1.2 * mm, "offsetDistance" : 25.4 * mm});
        }
        {
            var Q0;
            {var subQ0=sQuery(id+"F0.wireOp",EDGE,"E0.20");Q0=makeQuery(id+"F2.boolean.opBoolean","MERGE",FACE,{"derivedFrom":[makeQuery(id+"F1.opExtrude","SWEPT_FACE",FACE,{"disambiguationData":[OSD([subQ0])]}),makeQuery(id+"F2.opExtrude","SWEPT_FACE",FACE,{"disambiguationData":[OSD([subQ0])]})]});}
            extrude(context, id + "F34", {"entities" : qUnion([Q0]), "operationType" : NewBodyOperationType.ADD, "depth" : 1.2 * mm, "offsetDistance" : 25.4 * mm});
        }
        {
            var Q0;
            {var subQ0=sQuery(id+"F0.wireOp",EDGE,"E0.22");Q0=makeQuery(id+"F2.boolean.opBoolean","MERGE",FACE,{"derivedFrom":[makeQuery(id+"F1.opExtrude","SWEPT_FACE",FACE,{"disambiguationData":[OSD([subQ0])]}),makeQuery(id+"F2.opExtrude","SWEPT_FACE",FACE,{"disambiguationData":[OSD([subQ0])]})]});}
            extrude(context, id + "F35", {"entities" : qUnion([Q0]), "operationType" : NewBodyOperationType.ADD, "depth" : 1.2 * mm, "offsetDistance" : 25.4 * mm});
        }
        {
            var Q0;
            {var subQ0=sQuery(id+"F0.wireOp",EDGE,"E0.24");Q0=makeQuery(id+"F2.boolean.opBoolean","MERGE",FACE,{"derivedFrom":[makeQuery(id+"F1.opExtrude","SWEPT_FACE",FACE,{"disambiguationData":[OSD([subQ0])]}),makeQuery(id+"F2.opExtrude","SWEPT_FACE",FACE,{"disambiguationData":[OSD([subQ0])]})]});}
            extrude(context, id + "F36", {"entities" : qUnion([Q0]), "operationType" : NewBodyOperationType.ADD, "depth" : 1.2 * mm, "offsetDistance" : 25.4 * mm});
        }
        {
            var Q0;
            {var subQ0=sQuery(id+"F0.wireOp",EDGE,"E0.26");Q0=makeQuery(id+"F2.boolean.opBoolean","MERGE",FACE,{"derivedFrom":[makeQuery(id+"F1.opExtrude","SWEPT_FACE",FACE,{"disambiguationData":[OSD([subQ0])]}),makeQuery(id+"F2.opExtrude","SWEPT_FACE",FACE,{"disambiguationData":[OSD([subQ0])]})]});}
            extrude(context, id + "F37", {"entities" : qUnion([Q0]), "operationType" : NewBodyOperationType.ADD, "depth" : 1.2 * mm, "offsetDistance" : 25.4 * mm});
        }
        {
            var Q0;
            {var subQ0=sQuery(id+"F0.wireOp",EDGE,"E0.28");Q0=makeQuery(id+"F2.boolean.opBoolean","MERGE",FACE,{"derivedFrom":[makeQuery(id+"F1.opExtrude","SWEPT_FACE",FACE,{"disambiguationData":[OSD([subQ0])]}),makeQuery(id+"F2.opExtrude","SWEPT_FACE",FACE,{"disambiguationData":[OSD([subQ0])]})]});}
            extrude(context, id + "F38", {"entities" : qUnion([Q0]), "operationType" : NewBodyOperationType.ADD, "depth" : 1.2 * mm, "offsetDistance" : 25.4 * mm});
        }
        {
            var Q0;
            {var subQ0=sQuery(id+"F0.wireOp",EDGE,"E0.30");Q0=makeQuery(id+"F2.boolean.opBoolean","MERGE",FACE,{"derivedFrom":[makeQuery(id+"F1.opExtrude","SWEPT_FACE",FACE,{"disambiguationData":[OSD([subQ0])]}),makeQuery(id+"F2.opExtrude","SWEPT_FACE",FACE,{"disambiguationData":[OSD([subQ0])]})]});}
            extrude(context, id + "F39", {"entities" : qUnion([Q0]), "operationType" : NewBodyOperationType.ADD, "depth" : 1.2 * mm, "offsetDistance" : 25.4 * mm});
        }
        {
            var Q0;
            {var subQ0=sQuery(id+"F0.wireOp",EDGE,"E0.32");Q0=makeQuery(id+"F2.boolean.opBoolean","MERGE",FACE,{"derivedFrom":[makeQuery(id+"F1.opExtrude","SWEPT_FACE",FACE,{"disambiguationData":[OSD([subQ0])]}),makeQuery(id+"F2.opExtrude","SWEPT_FACE",FACE,{"disambiguationData":[OSD([subQ0])]})]});}
            extrude(context, id + "F40", {"entities" : qUnion([Q0]), "operationType" : NewBodyOperationType.ADD, "depth" : 1.2 * mm, "offsetDistance" : 25.4 * mm});
        }
        {
            var Q0;
            {var subQ0=sQuery(id+"F0.wireOp",EDGE,"E0.34");Q0=makeQuery(id+"F2.boolean.opBoolean","MERGE",FACE,{"derivedFrom":[makeQuery(id+"F1.opExtrude","SWEPT_FACE",FACE,{"disambiguationData":[OSD([subQ0])]}),makeQuery(id+"F2.opExtrude","SWEPT_FACE",FACE,{"disambiguationData":[OSD([subQ0])]})]});}
            extrude(context, id + "F41", {"entities" : qUnion([Q0]), "operationType" : NewBodyOperationType.ADD, "depth" : 1.2 * mm, "offsetDistance" : 25.4 * mm});
        }
        {
            var Q0;
            {var subQ0=sQuery(id+"F0.wireOp",EDGE,"E0.36");Q0=makeQuery(id+"F2.boolean.opBoolean","MERGE",FACE,{"derivedFrom":[makeQuery(id+"F1.opExtrude","SWEPT_FACE",FACE,{"disambiguationData":[OSD([subQ0])]}),makeQuery(id+"F2.opExtrude","SWEPT_FACE",FACE,{"disambiguationData":[OSD([subQ0])]})]});}
            extrude(context, id + "F42", {"entities" : qUnion([Q0]), "operationType" : NewBodyOperationType.ADD, "depth" : 1.2 * mm, "offsetDistance" : 25.4 * mm});
        }
        {
            var Q0;
            {var subQ0=sQuery(id+"F0.wireOp",EDGE,"E0.38");Q0=makeQuery(id+"F2.boolean.opBoolean","MERGE",FACE,{"derivedFrom":[makeQuery(id+"F1.opExtrude","SWEPT_FACE",FACE,{"disambiguationData":[OSD([subQ0])]}),makeQuery(id+"F2.opExtrude","SWEPT_FACE",FACE,{"disambiguationData":[OSD([subQ0])]})]});}
            extrude(context, id + "F43", {"entities" : qUnion([Q0]), "operationType" : NewBodyOperationType.ADD, "depth" : 1.2 * mm, "offsetDistance" : 25.4 * mm});
        }
        {
            var Q0;
            {var subQ0=sQuery(id+"F0.wireOp",EDGE,"E0.40");Q0=makeQuery(id+"F2.boolean.opBoolean","MERGE",FACE,{"derivedFrom":[makeQuery(id+"F1.opExtrude","SWEPT_FACE",FACE,{"disambiguationData":[OSD([subQ0])]}),makeQuery(id+"F2.opExtrude","SWEPT_FACE",FACE,{"disambiguationData":[OSD([subQ0])]})]});}
            extrude(context, id + "F44", {"entities" : qUnion([Q0]), "operationType" : NewBodyOperationType.ADD, "depth" : 1.2 * mm, "offsetDistance" : 25.4 * mm});
        }
        {
            var Q0;
            {var subQ0=sQuery(id+"F0.wireOp",EDGE,"E0.42");Q0=makeQuery(id+"F2.boolean.opBoolean","MERGE",FACE,{"derivedFrom":[makeQuery(id+"F1.opExtrude","SWEPT_FACE",FACE,{"disambiguationData":[OSD([subQ0])]}),makeQuery(id+"F2.opExtrude","SWEPT_FACE",FACE,{"disambiguationData":[OSD([subQ0])]})]});}
            extrude(context, id + "F45", {"entities" : qUnion([Q0]), "operationType" : NewBodyOperationType.ADD, "depth" : 1.2 * mm, "offsetDistance" : 25.4 * mm});
        }
        {
            var Q0;
            {var subQ0=sQuery(id+"F0.wireOp",EDGE,"E0.44");Q0=makeQuery(id+"F2.boolean.opBoolean","MERGE",FACE,{"derivedFrom":[makeQuery(id+"F1.opExtrude","SWEPT_FACE",FACE,{"disambiguationData":[OSD([subQ0])]}),makeQuery(id+"F2.opExtrude","SWEPT_FACE",FACE,{"disambiguationData":[OSD([subQ0])]})]});}
            extrude(context, id + "F46", {"entities" : qUnion([Q0]), "operationType" : NewBodyOperationType.ADD, "depth" : 1.2 * mm, "offsetDistance" : 25.4 * mm});
        }
        {
            var Q0;
            {var subQ0=sQuery(id+"F0.wireOp",EDGE,"E0.46");Q0=makeQuery(id+"F2.boolean.opBoolean","MERGE",FACE,{"derivedFrom":[makeQuery(id+"F1.opExtrude","SWEPT_FACE",FACE,{"disambiguationData":[OSD([subQ0])]}),makeQuery(id+"F2.opExtrude","SWEPT_FACE",FACE,{"disambiguationData":[OSD([subQ0])]})]});}
            extrude(context, id + "F47", {"entities" : qUnion([Q0]), "operationType" : NewBodyOperationType.ADD, "depth" : 1.2 * mm, "offsetDistance" : 25.4 * mm});
        }
        {
            var Q0;
            {var subQ0=sQuery(id+"F0.wireOp",EDGE,"E0.48");Q0=makeQuery(id+"F2.boolean.opBoolean","MERGE",FACE,{"derivedFrom":[makeQuery(id+"F1.opExtrude","SWEPT_FACE",FACE,{"disambiguationData":[OSD([subQ0])]}),makeQuery(id+"F2.opExtrude","SWEPT_FACE",FACE,{"disambiguationData":[OSD([subQ0])]})]});}
            extrude(context, id + "F48", {"entities" : qUnion([Q0]), "operationType" : NewBodyOperationType.ADD, "depth" : 1.2 * mm, "offsetDistance" : 25.4 * mm});
        }
        {
            var Q0;
            {var subQ0=sQuery(id+"F0.wireOp",EDGE,"E0.0");Q0=makeQuery(id+"F2.boolean.opBoolean","MERGE",FACE,{"derivedFrom":[makeQuery(id+"F1.opExtrude","SWEPT_FACE",FACE,{"disambiguationData":[OSD([subQ0])]}),makeQuery(id+"F2.opExtrude","SWEPT_FACE",FACE,{"disambiguationData":[OSD([subQ0])]})]});}
            extrude(context, id + "F49", {"entities" : qUnion([Q0]), "operationType" : NewBodyOperationType.ADD, "depth" : 1.2 * mm, "offsetDistance" : 25.4 * mm});
        }
        {
            var Q0;
            {var subQ0=sQuery(id+"F0.wireOp",EDGE,"E0.2");Q0=makeQuery(id+"F2.boolean.opBoolean","MERGE",FACE,{"derivedFrom":[makeQuery(id+"F1.opExtrude","SWEPT_FACE",FACE,{"disambiguationData":[OSD([subQ0])]}),makeQuery(id+"F2.opExtrude","SWEPT_FACE",FACE,{"disambiguationData":[OSD([subQ0])]})]});}
            extrude(context, id + "F50", {"entities" : qUnion([Q0]), "operationType" : NewBodyOperationType.ADD, "depth" : 1.2 * mm, "offsetDistance" : 25.4 * mm});
        }
        {
            var Q0;
            {var subQ0=sQuery(id+"F0.wireOp",EDGE,"E0.4");Q0=makeQuery(id+"F2.boolean.opBoolean","MERGE",FACE,{"derivedFrom":[makeQuery(id+"F1.opExtrude","SWEPT_FACE",FACE,{"disambiguationData":[OSD([subQ0])]}),makeQuery(id+"F2.opExtrude","SWEPT_FACE",FACE,{"disambiguationData":[OSD([subQ0])]})]});}
            extrude(context, id + "F51", {"entities" : qUnion([Q0]), "operationType" : NewBodyOperationType.ADD, "depth" : 1.2 * mm, "offsetDistance" : 25.4 * mm});
        }
        {
            var Q0;
            {var subQ0=sQuery(id+"F0.wireOp",EDGE,"E0.6");Q0=makeQuery(id+"F2.boolean.opBoolean","MERGE",FACE,{"derivedFrom":[makeQuery(id+"F1.opExtrude","SWEPT_FACE",FACE,{"disambiguationData":[OSD([subQ0])]}),makeQuery(id+"F2.opExtrude","SWEPT_FACE",FACE,{"disambiguationData":[OSD([subQ0])]})]});}
            extrude(context, id + "F52", {"entities" : qUnion([Q0]), "operationType" : NewBodyOperationType.ADD, "depth" : 1.2 * mm, "offsetDistance" : 25.4 * mm});
        }
        {
            var Q0;
            {var subQ0=sQuery(id+"F0.wireOp",EDGE,"E0.8");Q0=makeQuery(id+"F2.boolean.opBoolean","MERGE",FACE,{"derivedFrom":[makeQuery(id+"F1.opExtrude","SWEPT_FACE",FACE,{"disambiguationData":[OSD([subQ0])]}),makeQuery(id+"F2.opExtrude","SWEPT_FACE",FACE,{"disambiguationData":[OSD([subQ0])]})]});}
            extrude(context, id + "F53", {"entities" : qUnion([Q0]), "operationType" : NewBodyOperationType.ADD, "depth" : 1.2 * mm, "offsetDistance" : 25.4 * mm});
        }
        {
            var Q0;
            {var subQ0=sQuery(id+"F0.wireOp",EDGE,"E0.10");Q0=makeQuery(id+"F2.boolean.opBoolean","MERGE",FACE,{"derivedFrom":[makeQuery(id+"F1.opExtrude","SWEPT_FACE",FACE,{"disambiguationData":[OSD([subQ0])]}),makeQuery(id+"F2.opExtrude","SWEPT_FACE",FACE,{"disambiguationData":[OSD([subQ0])]})]});}
            extrude(context, id + "F54", {"entities" : qUnion([Q0]), "operationType" : NewBodyOperationType.ADD, "depth" : 1.2 * mm, "offsetDistance" : 25.4 * mm});
        }
        {
            var Q0;
            {var subQ0=sQuery(id+"F0.wireOp",EDGE,"E0.12");Q0=makeQuery(id+"F2.boolean.opBoolean","MERGE",FACE,{"derivedFrom":[makeQuery(id+"F1.opExtrude","SWEPT_FACE",FACE,{"disambiguationData":[OSD([subQ0])]}),makeQuery(id+"F2.opExtrude","SWEPT_FACE",FACE,{"disambiguationData":[OSD([subQ0])]})]});}
            extrude(context, id + "F55", {"entities" : qUnion([Q0]), "operationType" : NewBodyOperationType.ADD, "depth" : 1.2 * mm, "offsetDistance" : 25.4 * mm});
        }
        {
            var Q0;
            Q0=makeQuery(id+"F53.opExtrude","CAP_EDGE",EDGE,{"disambiguationData":[OSD([sQuery(id+"F0.wireOp",EDGE,"E0.7"),sQuery(id+"F0.wireOp",EDGE,"E0.8")])],"isStart":false});
            var Q1;
            Q1=makeQuery(id+"F53.opExtrude","CAP_EDGE",EDGE,{"disambiguationData":[OSD([sQuery(id+"F0.wireOp",EDGE,"E0.8"),sQuery(id+"F0.wireOp",EDGE,"E0.9")])],"isStart":false});
            var Q2;
            Q2=makeQuery(id+"F54.opExtrude","CAP_EDGE",EDGE,{"disambiguationData":[OSD([sQuery(id+"F0.wireOp",EDGE,"E0.10"),sQuery(id+"F0.wireOp",EDGE,"E0.11")])],"isStart":false});
            var Q3;
            Q3=makeQuery(id+"F54.opExtrude","CAP_EDGE",EDGE,{"disambiguationData":[OSD([sQuery(id+"F0.wireOp",EDGE,"E0.9"),sQuery(id+"F0.wireOp",EDGE,"E0.10")])],"isStart":false});
            var Q4;
            Q4=makeQuery(id+"F55.opExtrude","CAP_EDGE",EDGE,{"disambiguationData":[OSD([sQuery(id+"F0.wireOp",EDGE,"E0.11"),sQuery(id+"F0.wireOp",EDGE,"E0.12")])],"isStart":false});
            var Q5;
            Q5=makeQuery(id+"F55.opExtrude","CAP_EDGE",EDGE,{"disambiguationData":[OSD([sQuery(id+"F0.wireOp",EDGE,"E0.12"),sQuery(id+"F0.wireOp",EDGE,"E0.13")])],"isStart":false});
            var Q6;
            Q6=makeQuery(id+"F52.opExtrude","CAP_EDGE",EDGE,{"disambiguationData":[OSD([sQuery(id+"F0.wireOp",EDGE,"E0.6"),sQuery(id+"F0.wireOp",EDGE,"E0.7")])],"isStart":false});
            var Q7;
            Q7=makeQuery(id+"F52.opExtrude","CAP_EDGE",EDGE,{"disambiguationData":[OSD([sQuery(id+"F0.wireOp",EDGE,"E0.5"),sQuery(id+"F0.wireOp",EDGE,"E0.6")])],"isStart":false});
            var Q8;
            Q8=makeQuery(id+"F51.opExtrude","CAP_EDGE",EDGE,{"disambiguationData":[OSD([sQuery(id+"F0.wireOp",EDGE,"E0.4"),sQuery(id+"F0.wireOp",EDGE,"E0.5")])],"isStart":false});
            var Q9;
            Q9=makeQuery(id+"F51.opExtrude","CAP_EDGE",EDGE,{"disambiguationData":[OSD([sQuery(id+"F0.wireOp",EDGE,"E0.3"),sQuery(id+"F0.wireOp",EDGE,"E0.4")])],"isStart":false});
            var Q10;
            Q10=makeQuery(id+"F50.opExtrude","CAP_EDGE",EDGE,{"disambiguationData":[OSD([sQuery(id+"F0.wireOp",EDGE,"E0.2"),sQuery(id+"F0.wireOp",EDGE,"E0.3")])],"isStart":false});
            var Q11;
            Q11=makeQuery(id+"F50.opExtrude","CAP_EDGE",EDGE,{"disambiguationData":[OSD([sQuery(id+"F0.wireOp",EDGE,"E0.1"),sQuery(id+"F0.wireOp",EDGE,"E0.2")])],"isStart":false});
            var Q12;
            Q12=makeQuery(id+"F49.opExtrude","CAP_EDGE",EDGE,{"disambiguationData":[OSD([sQuery(id+"F0.wireOp",EDGE,"E0.0"),sQuery(id+"F0.wireOp",EDGE,"E0.1")])],"isStart":false});
            var Q13;
            Q13=makeQuery(id+"F49.opExtrude","CAP_EDGE",EDGE,{"disambiguationData":[OSD([sQuery(id+"F0.wireOp",EDGE,"E0.0"),sQuery(id+"F0.wireOp",EDGE,"E0.49")])],"isStart":false});
            var Q14;
            Q14=makeQuery(id+"F48.opExtrude","CAP_EDGE",EDGE,{"disambiguationData":[OSD([sQuery(id+"F0.wireOp",EDGE,"E0.48"),sQuery(id+"F0.wireOp",EDGE,"E0.49")])],"isStart":false});
            var Q15;
            Q15=makeQuery(id+"F48.opExtrude","CAP_EDGE",EDGE,{"disambiguationData":[OSD([sQuery(id+"F0.wireOp",EDGE,"E0.47"),sQuery(id+"F0.wireOp",EDGE,"E0.48")])],"isStart":false});
            var Q16;
            Q16=makeQuery(id+"F47.opExtrude","CAP_EDGE",EDGE,{"disambiguationData":[OSD([sQuery(id+"F0.wireOp",EDGE,"E0.46"),sQuery(id+"F0.wireOp",EDGE,"E0.47")])],"isStart":false});
            var Q17;
            Q17=makeQuery(id+"F47.opExtrude","CAP_EDGE",EDGE,{"disambiguationData":[OSD([sQuery(id+"F0.wireOp",EDGE,"E0.45"),sQuery(id+"F0.wireOp",EDGE,"E0.46")])],"isStart":false});
            var Q18;
            Q18=makeQuery(id+"F46.opExtrude","CAP_EDGE",EDGE,{"disambiguationData":[OSD([sQuery(id+"F0.wireOp",EDGE,"E0.44"),sQuery(id+"F0.wireOp",EDGE,"E0.45")])],"isStart":false});
            var Q19;
            Q19=makeQuery(id+"F46.opExtrude","CAP_EDGE",EDGE,{"disambiguationData":[OSD([sQuery(id+"F0.wireOp",EDGE,"E0.43"),sQuery(id+"F0.wireOp",EDGE,"E0.44")])],"isStart":false});
            var Q20;
            Q20=makeQuery(id+"F45.opExtrude","CAP_EDGE",EDGE,{"disambiguationData":[OSD([sQuery(id+"F0.wireOp",EDGE,"E0.42"),sQuery(id+"F0.wireOp",EDGE,"E0.43")])],"isStart":false});
            var Q21;
            Q21=makeQuery(id+"F45.opExtrude","CAP_EDGE",EDGE,{"disambiguationData":[OSD([sQuery(id+"F0.wireOp",EDGE,"E0.41"),sQuery(id+"F0.wireOp",EDGE,"E0.42")])],"isStart":false});
            var Q22;
            Q22=makeQuery(id+"F44.opExtrude","CAP_EDGE",EDGE,{"disambiguationData":[OSD([sQuery(id+"F0.wireOp",EDGE,"E0.40"),sQuery(id+"F0.wireOp",EDGE,"E0.41")])],"isStart":false});
            var Q23;
            Q23=makeQuery(id+"F44.opExtrude","CAP_EDGE",EDGE,{"disambiguationData":[OSD([sQuery(id+"F0.wireOp",EDGE,"E0.39"),sQuery(id+"F0.wireOp",EDGE,"E0.40")])],"isStart":false});
            var Q24;
            Q24=makeQuery(id+"F43.opExtrude","CAP_EDGE",EDGE,{"disambiguationData":[OSD([sQuery(id+"F0.wireOp",EDGE,"E0.38"),sQuery(id+"F0.wireOp",EDGE,"E0.39")])],"isStart":false});
            var Q25;
            Q25=makeQuery(id+"F43.opExtrude","CAP_EDGE",EDGE,{"disambiguationData":[OSD([sQuery(id+"F0.wireOp",EDGE,"E0.37"),sQuery(id+"F0.wireOp",EDGE,"E0.38")])],"isStart":false});
            var Q26;
            Q26=makeQuery(id+"F42.opExtrude","CAP_EDGE",EDGE,{"disambiguationData":[OSD([sQuery(id+"F0.wireOp",EDGE,"E0.36"),sQuery(id+"F0.wireOp",EDGE,"E0.37")])],"isStart":false});
            var Q27;
            Q27=makeQuery(id+"F42.opExtrude","CAP_EDGE",EDGE,{"disambiguationData":[OSD([sQuery(id+"F0.wireOp",EDGE,"E0.35"),sQuery(id+"F0.wireOp",EDGE,"E0.36")])],"isStart":false});
            var Q28;
            Q28=makeQuery(id+"F41.opExtrude","CAP_EDGE",EDGE,{"disambiguationData":[OSD([sQuery(id+"F0.wireOp",EDGE,"E0.34"),sQuery(id+"F0.wireOp",EDGE,"E0.35")])],"isStart":false});
            var Q29;
            Q29=makeQuery(id+"F41.opExtrude","CAP_EDGE",EDGE,{"disambiguationData":[OSD([sQuery(id+"F0.wireOp",EDGE,"E0.33"),sQuery(id+"F0.wireOp",EDGE,"E0.34")])],"isStart":false});
            var Q30;
            Q30=makeQuery(id+"F40.opExtrude","CAP_EDGE",EDGE,{"disambiguationData":[OSD([sQuery(id+"F0.wireOp",EDGE,"E0.32"),sQuery(id+"F0.wireOp",EDGE,"E0.33")])],"isStart":false});
            var Q31;
            Q31=makeQuery(id+"F40.opExtrude","CAP_EDGE",EDGE,{"disambiguationData":[OSD([sQuery(id+"F0.wireOp",EDGE,"E0.31"),sQuery(id+"F0.wireOp",EDGE,"E0.32")])],"isStart":false});
            var Q32;
            Q32=makeQuery(id+"F39.opExtrude","CAP_EDGE",EDGE,{"disambiguationData":[OSD([sQuery(id+"F0.wireOp",EDGE,"E0.30"),sQuery(id+"F0.wireOp",EDGE,"E0.31")])],"isStart":false});
            var Q33;
            Q33=makeQuery(id+"F39.opExtrude","CAP_EDGE",EDGE,{"disambiguationData":[OSD([sQuery(id+"F0.wireOp",EDGE,"E0.29"),sQuery(id+"F0.wireOp",EDGE,"E0.30")])],"isStart":false});
            var Q34;
            Q34=makeQuery(id+"F38.opExtrude","CAP_EDGE",EDGE,{"disambiguationData":[OSD([sQuery(id+"F0.wireOp",EDGE,"E0.28"),sQuery(id+"F0.wireOp",EDGE,"E0.29")])],"isStart":false});
            var Q35;
            Q35=makeQuery(id+"F38.opExtrude","CAP_EDGE",EDGE,{"disambiguationData":[OSD([sQuery(id+"F0.wireOp",EDGE,"E0.27"),sQuery(id+"F0.wireOp",EDGE,"E0.28")])],"isStart":false});
            var Q36;
            Q36=makeQuery(id+"F37.opExtrude","CAP_EDGE",EDGE,{"disambiguationData":[OSD([sQuery(id+"F0.wireOp",EDGE,"E0.25"),sQuery(id+"F0.wireOp",EDGE,"E0.26")])],"isStart":false});
            var Q37;
            Q37=makeQuery(id+"F37.opExtrude","CAP_EDGE",EDGE,{"disambiguationData":[OSD([sQuery(id+"F0.wireOp",EDGE,"E0.26"),sQuery(id+"F0.wireOp",EDGE,"E0.27")])],"isStart":false});
            var Q38;
            Q38=makeQuery(id+"F36.opExtrude","CAP_EDGE",EDGE,{"disambiguationData":[OSD([sQuery(id+"F0.wireOp",EDGE,"E0.24"),sQuery(id+"F0.wireOp",EDGE,"E0.25")])],"isStart":false});
            var Q39;
            Q39=makeQuery(id+"F36.opExtrude","CAP_EDGE",EDGE,{"disambiguationData":[OSD([sQuery(id+"F0.wireOp",EDGE,"E0.23"),sQuery(id+"F0.wireOp",EDGE,"E0.24")])],"isStart":false});
            var Q40;
            Q40=makeQuery(id+"F35.opExtrude","CAP_EDGE",EDGE,{"disambiguationData":[OSD([sQuery(id+"F0.wireOp",EDGE,"E0.22"),sQuery(id+"F0.wireOp",EDGE,"E0.23")])],"isStart":false});
            var Q41;
            Q41=makeQuery(id+"F35.opExtrude","CAP_EDGE",EDGE,{"disambiguationData":[OSD([sQuery(id+"F0.wireOp",EDGE,"E0.21"),sQuery(id+"F0.wireOp",EDGE,"E0.22")])],"isStart":false});
            var Q42;
            Q42=makeQuery(id+"F34.opExtrude","CAP_EDGE",EDGE,{"disambiguationData":[OSD([sQuery(id+"F0.wireOp",EDGE,"E0.20"),sQuery(id+"F0.wireOp",EDGE,"E0.21")])],"isStart":false});
            var Q43;
            Q43=makeQuery(id+"F34.opExtrude","CAP_EDGE",EDGE,{"disambiguationData":[OSD([sQuery(id+"F0.wireOp",EDGE,"E0.19"),sQuery(id+"F0.wireOp",EDGE,"E0.20")])],"isStart":false});
            var Q44;
            Q44=makeQuery(id+"F33.opExtrude","CAP_EDGE",EDGE,{"disambiguationData":[OSD([sQuery(id+"F0.wireOp",EDGE,"E0.18"),sQuery(id+"F0.wireOp",EDGE,"E0.19")])],"isStart":false});
            var Q45;
            Q45=makeQuery(id+"F33.opExtrude","CAP_EDGE",EDGE,{"disambiguationData":[OSD([sQuery(id+"F0.wireOp",EDGE,"E0.17"),sQuery(id+"F0.wireOp",EDGE,"E0.18")])],"isStart":false});
            var Q46;
            Q46=makeQuery(id+"F31.opExtrude","CAP_EDGE",EDGE,{"disambiguationData":[OSD([sQuery(id+"F0.wireOp",EDGE,"E0.16"),sQuery(id+"F0.wireOp",EDGE,"E0.17")])],"isStart":false});
            var Q47;
            Q47=makeQuery(id+"F31.opExtrude","CAP_EDGE",EDGE,{"disambiguationData":[OSD([sQuery(id+"F0.wireOp",EDGE,"E0.15"),sQuery(id+"F0.wireOp",EDGE,"E0.16")])],"isStart":false});
            var Q48;
            Q48=makeQuery(id+"F32.opExtrude","CAP_EDGE",EDGE,{"disambiguationData":[OSD([sQuery(id+"F0.wireOp",EDGE,"E0.13"),sQuery(id+"F0.wireOp",EDGE,"E0.14")])],"isStart":false});
            var Q49;
            Q49=makeQuery(id+"F32.opExtrude","CAP_EDGE",EDGE,{"disambiguationData":[OSD([sQuery(id+"F0.wireOp",EDGE,"E0.14"),sQuery(id+"F0.wireOp",EDGE,"E0.15")])],"isStart":false});
            chamfer(context, id + "F56", {"entities" : qUnion([Q0, Q1, Q2, Q3, Q4, Q5, Q6, Q7, Q8, Q9, Q10, Q11, Q12, Q13, Q14, Q15, Q16, Q17, Q18, Q19, Q20, Q21, Q22, Q23, Q24, Q25, Q26, Q27, Q28, Q29, Q30, Q31, Q32, Q33, Q34, Q35, Q36, Q37, Q38, Q39, Q40, Q41, Q42, Q43, Q44, Q45, Q46, Q47, Q48, Q49]), "width" : 1.2 * mm, "tangentPropagation" : true});
        }
        {
            var Q0;
            Q0=qCreatedBy(makeId("Front.planeOp"),FACE);
            var sketch = newSketch(context, id + "F57", { "sketchPlane" : qUnion([Q0])});
            skPoint(sketch, "E4", {"position": v(12.48, 0) * mm});
            skPoint(sketch, "E5", {"position": v(7.16, 0) * mm});
            skPoint(sketch, "E6.0.midPoint", {"position": v(3.9, -4.64) * mm});
            skCircle(sketch, "E7", {"center": v(-7.92, 9.43) * mm, "radius": 2.18 * mm});
            skCircle(sketch, "E8", {"center": v(12.13, 2.15) * mm, "radius": 2.18 * mm});
            skCircle(sketch, "E9", {"center": v(-4.34, -11.43) * mm, "radius": 2.18 * mm});
            skPoint(sketch, "E6.cCircle.center.orphan", {"position": v(0, 0) * mm});
            skCircle(sketch, "E10", {"center": v(0, 0) * mm, "radius": 12.3 * mm});
            skSolve(sketch);
        }
        {
            var Q0;
            Q0=makeQuery(id+"F57.imprint","IMPRINT",FACE,{"disambiguationData":[TD([[makeQuery(id+"F57.imprint","IMPRINT",EDGE,{"derivedFrom":sQuery(id+"F57.wireOp",EDGE,"E8")}),1.0]])]});
            var Q1;
            Q1=makeQuery(id+"F57.imprint","IMPRINT",FACE,{"disambiguationData":[TD([[makeQuery(id+"F57.imprint","IMPRINT",EDGE,{"derivedFrom":sQuery(id+"F57.wireOp",EDGE,"E7")}),1.0]])]});
            var Q2;
            Q2=makeQuery(id+"F57.imprint","IMPRINT",FACE,{"disambiguationData":[TD([[makeQuery(id+"F57.imprint","IMPRINT",EDGE,{"derivedFrom":sQuery(id+"F57.wireOp",EDGE,"E9")}),1.0]])]});
            extrude(context, id + "F58", {"entities" : qUnion([Q0, Q1, Q2]), "operationType" : NewBodyOperationType.ADD, "depth" : 9.52 * mm, "offsetDistance" : 25.4 * mm});
        }
        {
            var Q0;
            Q0=makeQuery(id+"F0.imprint","IMPRINT",FACE,{"disambiguationData":[TD([[makeQuery(id+"F0.imprint","IMPRINT",EDGE,{"derivedFrom":sQuery(id+"F0.wireOp",EDGE,"E2")}),-1.0]])]});
            extrude(context, id + "F59", {"entities" : qUnion([Q0]), "oppositeDirection" : true, "depth" : 2.72 * mm, "offsetDistance" : 25.4 * mm});
        }
        {
            var Q0;
            Q0=qCreatedBy(makeId("Front.planeOp"),FACE);
            var sketch = newSketch(context, id + "F60", { "sketchPlane" : qUnion([Q0])});
            skLineSegment(sketch, "E11.1", {"start": v(-21.56, 9.44) * mm, "end": v(-21.46, 9.45) * mm});
            skLineSegment(sketch, "E11.2", {"start": v(18.95, 13.95) * mm, "end": v(18.93, 13.9) * mm});
            skPoint(sketch, "E11.0.midPoint", {"position": v(-9.48, -6.97) * mm});
            skLineSegment(sketch, "E12", {"start": v(-18.1, 8.1) * mm, "end": v(-32.93, 14.08) * mm});
            skCircle(sketch, "E13", {"center": v(0, 0) * mm, "radius": 34.54 * mm});
            skLineSegment(sketch, "E14", {"start": v(2.21, -20.56) * mm, "end": v(4.13, -34.3) * mm});
            skLineSegment(sketch, "E15", {"start": v(16.46, 12.1) * mm, "end": v(27.88, 20.4) * mm});
            skLineSegment(sketch, "E16.trimOffspring", {"start": v(2.6, -23.38) * mm, "end": v(2.6, -23.39) * mm});
            skCircle(sketch, "E17", {"center": v(0, 0) * mm, "radius": 35.81 * mm});
            skSolve(sketch);
        }
        {
            var Q0;
            Q0=sQuery(id+"F60.wireOp",EDGE,"E12");
            extrude(context, id + "F61", {"bodyType" : ToolBodyType.SURFACE, "surfaceEntities" : qUnion([Q0]), "depth" : 9.52 * mm, "offsetDistance" : 25.4 * mm});
        }
        {
            var Q0;
            Q0=sQuery(id+"F60.wireOp",EDGE,"E15");
            extrude(context, id + "F62", {"bodyType" : ToolBodyType.SURFACE, "surfaceEntities" : qUnion([Q0]), "depth" : 9.52 * mm, "offsetDistance" : 25.4 * mm});
        }
        {
            var Q0;
            Q0=sQuery(id+"F60.wireOp",EDGE,"E14");
            extrude(context, id + "F63", {"bodyType" : ToolBodyType.SURFACE, "surfaceEntities" : qUnion([Q0]), "depth" : 9.52 * mm, "offsetDistance" : 25.4 * mm});
        }
        {
            var Q0;
            Q0=makeQuery(id+"F60.imprint","IMPRINT",FACE,{"disambiguationData":[TD([[makeQuery(id+"F60.imprint","IMPRINT",EDGE,{"derivedFrom":sQuery(id+"F60.wireOp",EDGE,"E17")}),1.0]])]});
            extrude(context, id + "F64", {"entities" : qUnion([Q0]), "depth" : 9.52 * mm, "offsetDistance" : 25.4 * mm});
        }
        {
            var Q0;
            Q0=makeQuery(id+"F62.opExtrude","SWEPT_FACE",FACE,{"disambiguationData":[OSD([sQuery(id+"F60.wireOp",EDGE,"E15")])]});
            var Q1;
            Q1=makeQuery(id+"F61.opExtrude","SWEPT_FACE",FACE,{"disambiguationData":[OSD([sQuery(id+"F60.wireOp",EDGE,"E12")])]});
            var Q2;
            Q2=makeQuery(id+"F63.opExtrude","SWEPT_FACE",FACE,{"disambiguationData":[OSD([sQuery(id+"F60.wireOp",EDGE,"E14")])]});
            extrude(context, id + "F65", {"entities" : qUnion([Q0, Q1, Q2]), "depth" : 1.59 * mm, "offsetDistance" : 25.4 * mm});
        }
        {
            var Q0;
            Q0=makeQuery(id+"F59.opExtrude","CAP_FACE",FACE,{"disambiguationData":[OSD([sQuery(id+"F0.wireOp",EDGE,"E2"),sQuery(id+"F0.wireOp",EDGE,"E3")])],"isStart":false});
            var sketch = newSketch(context, id + "F66", { "sketchPlane" : qUnion([Q0])});
            skPoint(sketch, "E18", {"position": v(4.43, -11.5) * mm});
            skPoint(sketch, "E19", {"position": v(-12.16, 2.13) * mm});
            skPoint(sketch, "E20", {"position": v(8.03, 9.7) * mm});
            skSolve(sketch);
        }
        {
            var Q0;
            Q0=sQuery(id+"F66.wireOp",VERTEX,"E18");
            var Q1;
            Q1=makeQuery(id+"F58.opExtrude","SWEPT_BODY",BODY,{"disambiguationData":[OSD([sQuery(id+"F57.wireOp",EDGE,"E9")])]});
            var Q2;
            Q2=makeQuery(id+"F59.opExtrude","SWEPT_BODY",BODY,{"disambiguationData":[OSD([sQuery(id+"F0.wireOp",EDGE,"E2"),sQuery(id+"F0.wireOp",EDGE,"E3")])]});
            hole(context, id + "F67", {"style" : HoleStyle.SIMPLE, "endStyle" : HoleEndStyle.THROUGH, "holeDiameter" : 1.59 * mm, "majorDiameter" : 6.35 * mm, "isTappedThrough" : true, "tappedDepth" : 12.7 * mm, "tapClearance" : 3, "locations" : qUnion([Q0]), "scope" : qUnion([Q1, Q2])});
        }
        {
            var Q0;
            Q0=sQuery(id+"F57.wireOp",VERTEX,"E8.center");
            var Q1;
            Q1=makeQuery(id+"F58.opExtrude","SWEPT_BODY",BODY,{"disambiguationData":[OSD([sQuery(id+"F57.wireOp",EDGE,"E8")])]});
            var Q2;
            Q2=makeQuery(id+"F59.opExtrude","SWEPT_BODY",BODY,{"disambiguationData":[OSD([sQuery(id+"F0.wireOp",EDGE,"E2"),sQuery(id+"F0.wireOp",EDGE,"E3")])]});
            hole(context, id + "F68", {"style" : HoleStyle.SIMPLE, "endStyle" : HoleEndStyle.THROUGH, "holeDiameter" : 1.59 * mm, "majorDiameter" : 6.35 * mm, "isTappedThrough" : true, "tappedDepth" : 12.7 * mm, "tapClearance" : 3, "locations" : qUnion([Q0]), "scope" : qUnion([Q1, Q2])});
        }
        {
            var Q0;
            Q0=sQuery(id+"F57.wireOp",VERTEX,"E7.center");
            var Q1;
            Q1=makeQuery(id+"F59.opExtrude","SWEPT_BODY",BODY,{"disambiguationData":[OSD([sQuery(id+"F0.wireOp",EDGE,"E2"),sQuery(id+"F0.wireOp",EDGE,"E3")])]});
            hole(context, id + "F69", {"style" : HoleStyle.SIMPLE, "endStyle" : HoleEndStyle.THROUGH, "holeDiameter" : 1.59 * mm, "majorDiameter" : 6.35 * mm, "isTappedThrough" : true, "tappedDepth" : 12.7 * mm, "tapClearance" : 3, "locations" : qUnion([Q0]), "scope" : qUnion([Q1])});
        }
        {
            var Q0;
            Q0=makeQuery(id+"F3.opExtrude","CAP_FACE",FACE,{"disambiguationData":[OSD([sQuery(id+"F0.wireOp",EDGE,"E2")])],"isStart":false});
            cPlane(context, id + "F70", {"entities" : qUnion([Q0]), "cplaneType" : CPlaneType.OFFSET, "offset" : 76.2 * mm, "oppositeDirection" : true, "width" : 152.4 * mm, "height" : 152.4 * mm});
        }
        {
            var Q0;
            Q0=qCreatedBy(id+"F70.planeOp",FACE);
            var sketch = newSketch(context, id + "F71", { "sketchPlane" : qUnion([Q0])});
            skPoint(sketch, "E21", {"position": v(0, 0) * mm});
            skSolve(sketch);
        }
        {
            var Q0;
            Q0=sQuery(id+"F71.wireOp",VERTEX,"E21");
            var Q1;
            Q1=makeQuery(id+"F3.opExtrude","SWEPT_BODY",BODY,{"disambiguationData":[OSD([sQuery(id+"F0.wireOp",EDGE,"E2")])]});
            hole(context, id + "F72", {"style" : HoleStyle.SIMPLE, "endStyle" : HoleEndStyle.THROUGH, "holeDiameter" : 1.59 * mm, "majorDiameter" : 6.35 * mm, "isTappedThrough" : true, "tappedDepth" : 12.7 * mm, "tapClearance" : 3, "locations" : qUnion([Q0]), "scope" : qUnion([Q1])});
        }
    });
